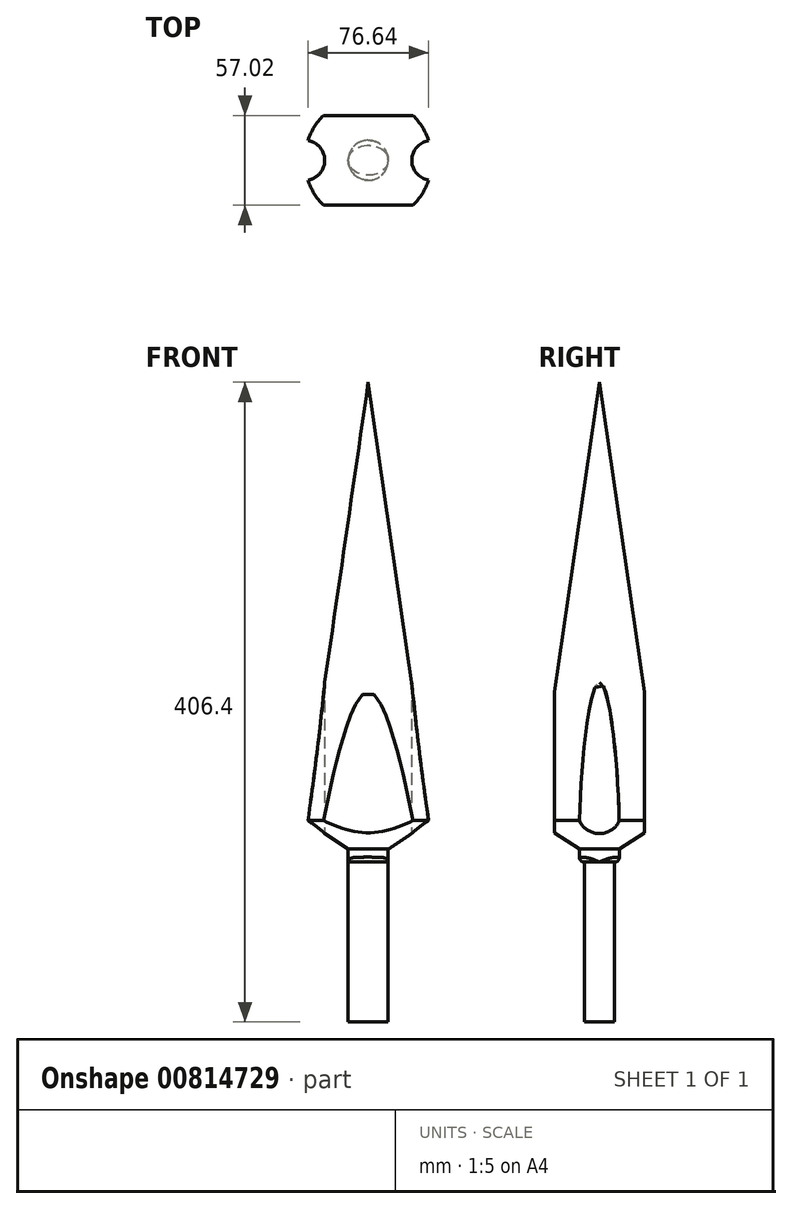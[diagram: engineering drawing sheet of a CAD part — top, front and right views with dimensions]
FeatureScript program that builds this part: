
annotation { "Feature Type Name" : "Feature", "Feature Type Description" : "" }
export const myFeature = defineFeature(function(context is Context, id is Id, definition is map)
    precondition{}
    {
        {
            var Q0;
            Q0=qCreatedBy(makeId("Front.planeOp"),FACE);
            var sketch = newSketch(context, id + "F0", { "sketchPlane" : qUnion([Q0])});
            skLineSegment(sketch, "E0", {"start": v(0, 0) * mm, "end": v(0, 304.8) * mm});
            skLineSegment(sketch, "E1", {"start": v(0, 0) * mm, "end": v(0, -63.5) * mm, "construction": true});
            skLineSegment(sketch, "E2", {"start": v(-12.7, 8.32) * mm, "end": v(-40.32, 26.42) * mm});
            skLineSegment(sketch, "E3", {"start": v(-40.32, 26.42) * mm, "end": v(0, 304.8) * mm});
            skLineSegment(sketch, "E4", {"start": v(0, 0) * mm, "end": v(-12.7, 0) * mm});
            skLineSegment(sketch, "E5", {"start": v(-12.7, 0) * mm, "end": v(-12.7, 8.32) * mm});
            skSolve(sketch);
        }
        {
            var Q0;
            Q0 = qSketchRegion(id + "F0", true);
            var Q1;
            Q1=sQuery(id+"F0.wireOp",EDGE,"E1");
            revolve(context, id + "F1", {"surfaceOperationType" : NewSurfaceOperationType.NEW, "entities" : qUnion([Q0]), "axis" : qUnion([Q1]), "revolveType" : RevolveType.FULL});
        }
        {
            var Q0;
            Q0=qCreatedBy(makeId("Top.planeOp"),FACE);
            var sketch = newSketch(context, id + "F2", { "sketchPlane" : qUnion([Q0])});
            skCircle(sketch, "E6.0", {"center": v(0, 0) * mm, "radius": 40.32 * mm, "construction": true});
            skLineSegment(sketch, "E7", {"start": v(0, 0) * mm, "end": v(0, -40.32) * mm, "construction": true});
            skLineSegment(sketch, "E8", {"start": v(0, 0) * mm, "end": v(-28.5, -28.5) * mm, "construction": true});
            skLineSegment(sketch, "E9.bottom", {"start": v(-28.5, -28.5) * mm, "end": v(28.5, -28.5) * mm});
            skLineSegment(sketch, "E9.top", {"start": v(-28.5, -52.13) * mm, "end": v(28.5, -52.13) * mm});
            skLineSegment(sketch, "E9.left", {"start": v(-28.5, -28.5) * mm, "end": v(-28.5, -52.13) * mm});
            skLineSegment(sketch, "E9.right", {"start": v(28.5, -28.5) * mm, "end": v(28.5, -52.13) * mm});
            skPoint(sketch, "E9.middle", {"position": v(0, -40.32) * mm});
            skLineSegment(sketch, "E10", {"start": v(0, 0) * mm, "end": v(18.52, 0) * mm, "construction": true});
            skLineSegment(sketch, "E11.MirrorCS", {"start": v(-28.5, 28.5) * mm, "end": v(28.5, 28.5) * mm});
            skLineSegment(sketch, "E12.MirrorCS", {"start": v(28.5, 28.5) * mm, "end": v(28.5, 52.13) * mm});
            skLineSegment(sketch, "E13.MirrorCS", {"start": v(-28.5, 52.13) * mm, "end": v(28.5, 52.13) * mm});
            skLineSegment(sketch, "E14.MirrorCS", {"start": v(-28.5, 28.5) * mm, "end": v(-28.5, 52.13) * mm});
            skCircle(sketch, "E15", {"center": v(40.32, 0) * mm, "radius": 12.7 * mm});
            skCircle(sketch, "E16.MirrorC", {"center": v(-40.32, 0) * mm, "radius": 12.7 * mm});
            skSolve(sketch);
        }
        {
            var Q0;
            Q0 = qSketchRegion(id + "F2", true);
            extrude(context, id + "F3", {"entities" : qUnion([Q0]), "operationType" : NewBodyOperationType.REMOVE, "endBound" : BoundingType.THROUGH_ALL, "depth" : 25.4 * mm, "offsetDistance" : 25.4 * mm});
        }
        {
            var Q0;
            Q0=makeQuery(id+"F1.opRevolve","SWEPT_FACE",FACE,{"disambiguationData":[OSD([sQuery(id+"F0.wireOp",EDGE,"E4")])]});
            var sketch = newSketch(context, id + "F4", { "sketchPlane" : qUnion([Q0])});
            skEllipse(sketch, "E17", {"center": v(0, 0) * mm, "majorRadius": 12.7 * mm, "minorRadius": 9.53 * mm, "majorAxis": v(1, 0)});
            skSolve(sketch);
        }
        {
            var Q0;
            Q0 = qSketchRegion(id + "F4", true);
            extrude(context, id + "F5", {"entities" : qUnion([Q0]), "operationType" : NewBodyOperationType.ADD, "depth" : 101.6 * mm, "offsetDistance" : 25.4 * mm});
        }
        {
            var Q0;
            Q0=makeQuery(id+"F5.boolean.opBoolean","SPLIT",EDGE,{"disambiguationData":[OD(0.0)],"derivedFrom":makeQuery(id+"F1.opRevolve","SWEPT_EDGE",EDGE,{"disambiguationData":[OSD([sQuery(id+"F0.wireOp",EDGE,"E4"),sQuery(id+"F0.wireOp",EDGE,"E5")])]})});
            var Q1;
            Q1=makeQuery(id+"F5.boolean.opBoolean","SPLIT",EDGE,{"disambiguationData":[OD(1.0)],"derivedFrom":makeQuery(id+"F1.opRevolve","SWEPT_EDGE",EDGE,{"disambiguationData":[OSD([sQuery(id+"F0.wireOp",EDGE,"E4"),sQuery(id+"F0.wireOp",EDGE,"E5")])]})});
            fillet(context, id + "F6", {"entities" : qUnion([Q0, Q1]), "radius" : 3.17 * mm, "tangentPropagation" : true, "allowEdgeOverflow" : false});
        }
    });
